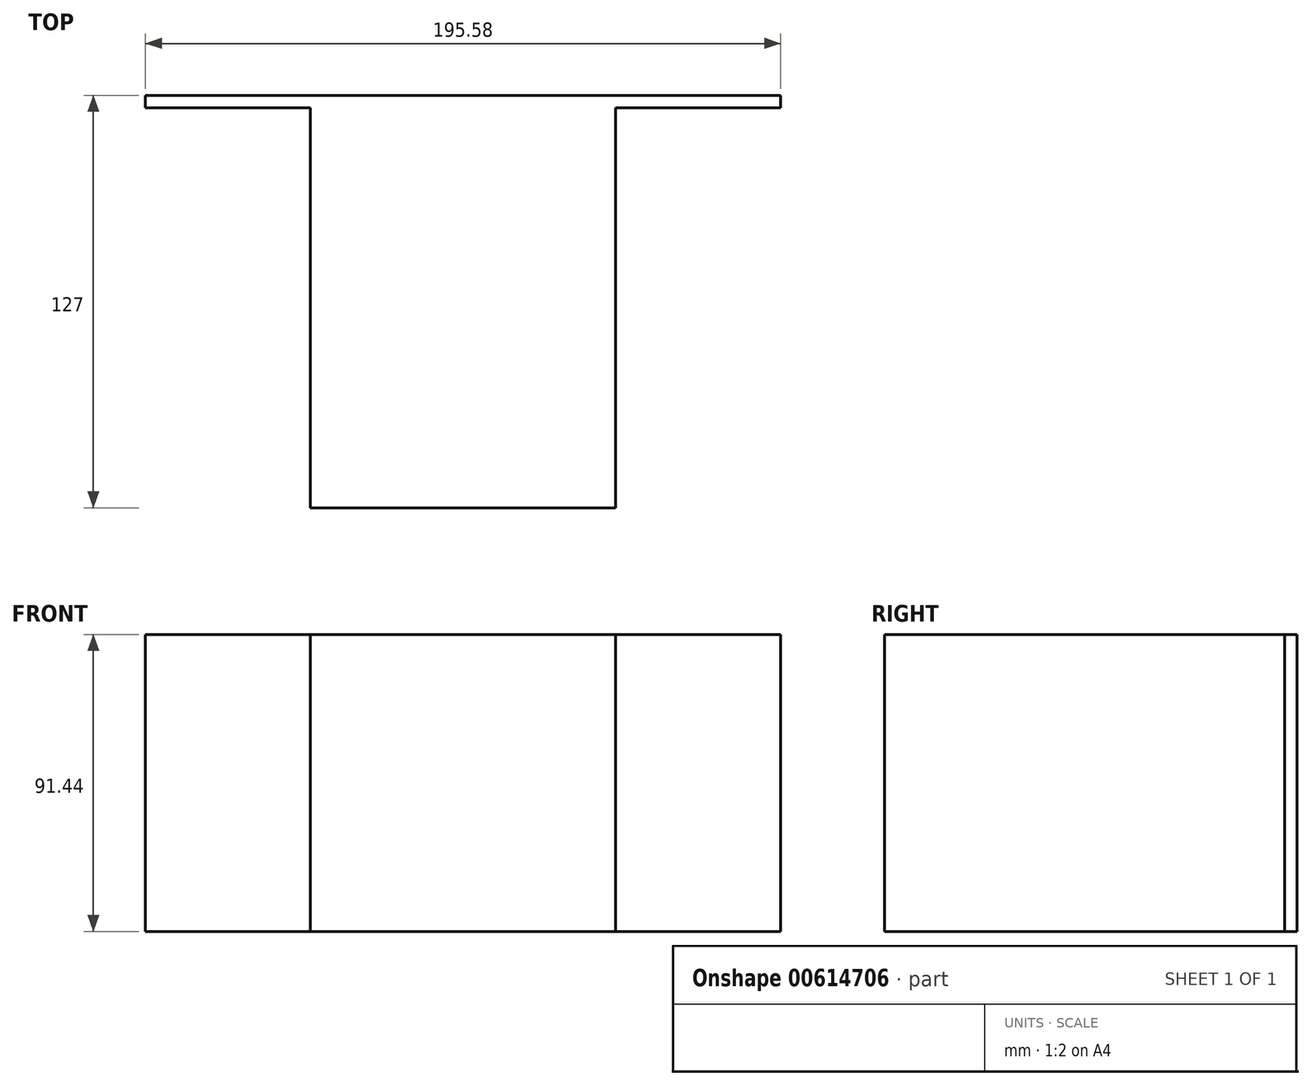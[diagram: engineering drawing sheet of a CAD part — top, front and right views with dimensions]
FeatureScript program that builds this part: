
annotation { "Feature Type Name" : "Feature", "Feature Type Description" : "" }
export const myFeature = defineFeature(function(context is Context, id is Id, definition is map)
    precondition{}
    {
        {
            var Q0;
            Q0=qCreatedBy(makeId("Front.planeOp"),FACE);
            var sketch = newSketch(context, id + "F0", { "sketchPlane" : qUnion([Q0])});
            skLineSegment(sketch, "E0.bottom", {"start": v(0, 0) * mm, "end": v(195.58, 0) * mm});
            skLineSegment(sketch, "E0.top", {"start": v(0, 91.44) * mm, "end": v(195.58, 91.44) * mm});
            skLineSegment(sketch, "E0.left", {"start": v(0, 0) * mm, "end": v(0, 91.44) * mm});
            skLineSegment(sketch, "E0.right", {"start": v(195.58, 0) * mm, "end": v(195.58, 91.44) * mm});
            skSolve(sketch);
        }
        {
            var Q0;
            Q0 = qSketchRegion(id + "F0", true);
            extrude(context, id + "F1", {"entities" : qUnion([Q0]), "oppositeDirection" : true, "depth" : 127 * mm, "offsetDistance" : 25.4 * mm});
        }
        {
            var Q0;
            Q0=makeQuery(id+"F1.opExtrude","CAP_FACE",FACE,{"disambiguationData":[OSD([sQuery(id+"F0.wireOp",EDGE,"E0.bottom"),sQuery(id+"F0.wireOp",EDGE,"E0.top"),sQuery(id+"F0.wireOp",EDGE,"E0.left"),sQuery(id+"F0.wireOp",EDGE,"E0.right")])],"isStart":true});
            var sketch = newSketch(context, id + "F2", { "sketchPlane" : qUnion([Q0])});
            skLineSegment(sketch, "E1.bottom", {"start": v(50.8, 0) * mm, "end": v(144.78, 0) * mm});
            skLineSegment(sketch, "E1.top", {"start": v(50.8, 91.44) * mm, "end": v(144.78, 91.44) * mm});
            skLineSegment(sketch, "E1.left", {"start": v(50.8, 0) * mm, "end": v(50.8, 91.44) * mm});
            skLineSegment(sketch, "E1.right", {"start": v(144.78, 0) * mm, "end": v(144.78, 91.44) * mm});
            skSolve(sketch);
        }
        {
            var Q0;
            {var subQ0=sQuery(id+"F2.wireOp",EDGE,"E1.left");Q0=makeQuery(id+"F2.imprint","IMPRINT",FACE,{"disambiguationData":[TD([[makeQuery(id+"F2.imprint","IMPRINT",EDGE,{"derivedFrom":subQ0}),1.0]])]});}
            var Q1;
            {var subQ0=sQuery(id+"F2.wireOp",EDGE,"E1.right");Q1=makeQuery(id+"F2.imprint","IMPRINT",FACE,{"disambiguationData":[TD([[makeQuery(id+"F2.imprint","IMPRINT",EDGE,{"derivedFrom":subQ0}),-1.0]])]});}
            extrude(context, id + "F3", {"entities" : qUnion([Q0, Q1]), "operationType" : NewBodyOperationType.REMOVE, "oppositeDirection" : true, "depth" : 123.19 * mm, "offsetDistance" : 25.4 * mm});
        }
    });
